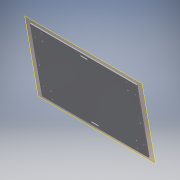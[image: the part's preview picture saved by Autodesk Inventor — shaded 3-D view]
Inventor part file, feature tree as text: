
AUTODESK INVENTOR PART (.ipt)
format: ipt  version: 2019 (Build 230136000, 136)  size: 235,520 bytes
history: native  units: in
note: dims shown in document units (in); Inventor stores cm internally (conversion verified against a paired STEP export)
features: reference x36, other x11, extrude x2, fillet x2, hole x2, sketch x1
ambient origin geometry x8: Origin, YZ Plane, XZ Plane, XY Plane, X Axis, Y Axis, Z Axis, Center Point
bodies: Solid1 (feature_tree)
feature tree (54):
  other  "10DegOffset"
  extrude  "Panel"  Depth=0.0394in
  fillet  "CornerFillets"  Radius=0.1495in
  hole  "ScrewHoles"  [1 undecoded]
  extrude  "TabSlotExtrusion"  Depth=0.149in
  fillet  "TabSlotFillets"  Radius=1.054in
  hole  "FeetMountingHole"  [1 undecoded]
  other  "BottomDimensions"
  reference  "Reference1"
  reference  "Reference2"
  reference  "Reference3"
  reference  "Reference4"
  other  "ScrewHoleSketch"
  reference  "Reference5"
  reference  "Reference6"
  reference  "Reference7"
  reference  "Reference8"
  reference  "Reference9"
  reference  "Reference10"
  reference  "Reference13"
  reference  "Reference14"
  reference  "Reference15"
  reference  "Reference16"
  reference  "Reference17"
  reference  "Reference18"
  reference  "Reference19"
  reference  "Reference20"
  reference  "Reference23"
  reference  "Reference24"
  other  "TabSlotSketch"
  reference  "Reference27"
  reference  "Reference28"
  reference  "Reference29"
  reference  "Reference30"
  reference  "Reference33"
  reference  "Reference34"
  reference  "Reference35"
  reference  "Reference36"
  reference  "Reference41"
  reference  "Reference42"
  reference  "Reference43"
  reference  "Reference44"
  reference  "Reference47"
  reference  "Reference48"
  reference  "Reference49"
  reference  "Reference50"
  sketch  "Sketch4"  dims[d0=0.125in d1=0.0in d2=0.0394in d3=0.1495in d4=0.75in d5=0.375in d6=0.25in d7=0.5635in d8=1.0in d9=0.8108in d10=1.054in d12=0.149in d13=1.054in d14=0.149in d15=1.054in d16=0.149in d17=1.054in d18=0.149in d19=0.125in d20=0.0in d21=0.0197in d22=0.1875in d23=0.75in d24=0.375in d25=0.25in d26=0.5635in d27=1.0in d28=0.8108in]
  parser-record x1  (decoder bookkeeping rows leaked as tree rows — omitted from the tree; the rows remain in map.json)
  other  "ArcadeController.iam"
  other  "TopPanel:1"
  other  "Panel_side:2"
  other  "Panel_back:1"
  other  "Panel_side:1"
  other  "Panel_front:1"
note: 2 required parameter values undecoded (feature->parameter linkage not recoverable at this tier; creation-order binding heuristic only, values carry confidence <= 0.55)
note: 1 file-system path scrubbed to <path> (originals preserved in map.json)
